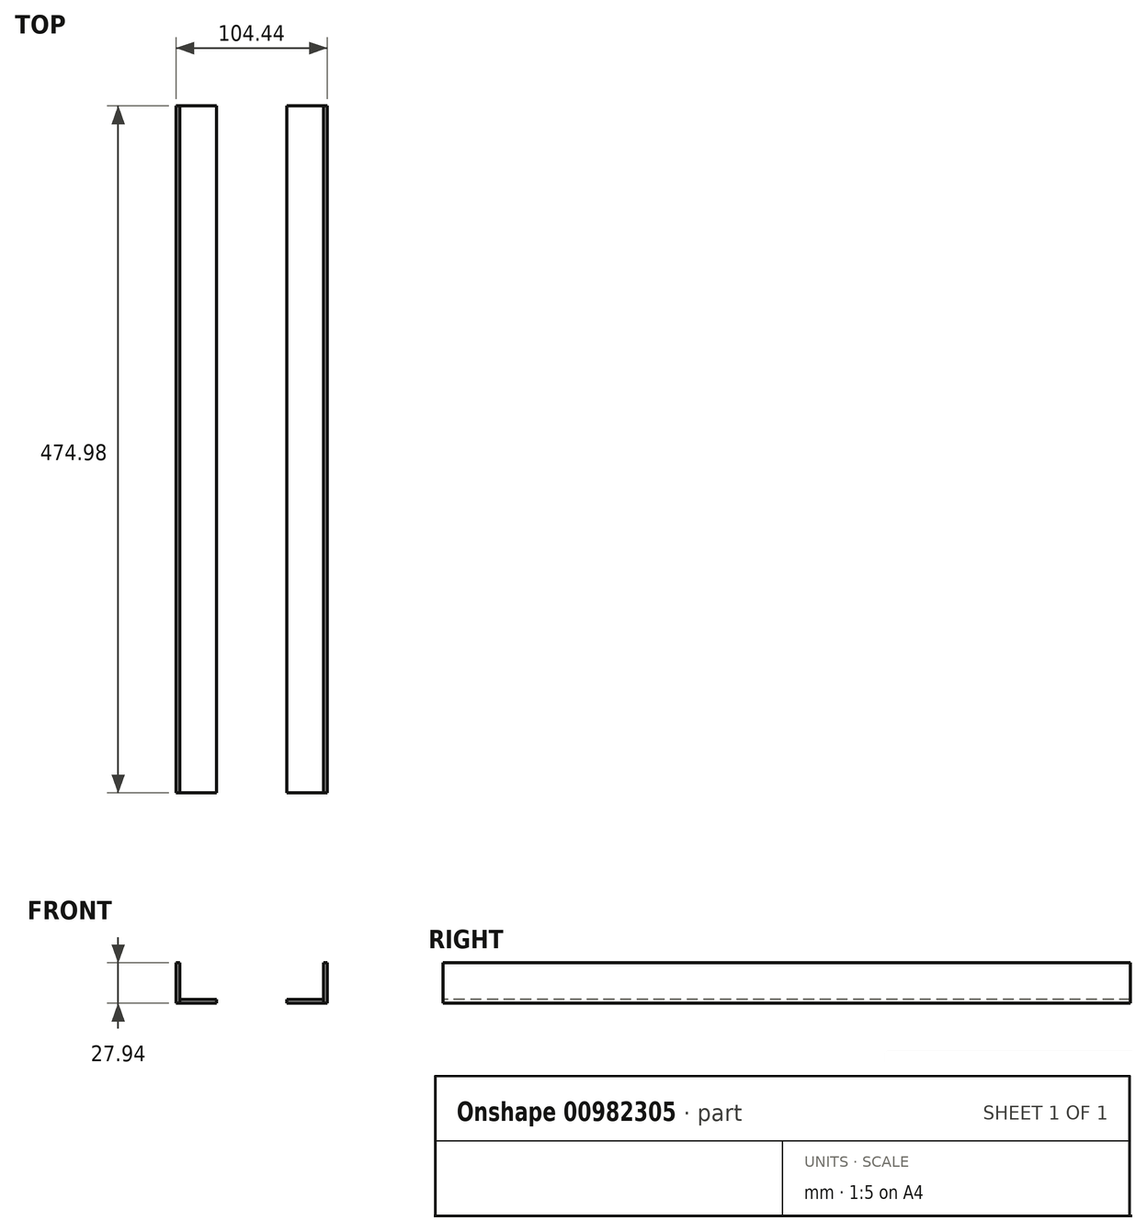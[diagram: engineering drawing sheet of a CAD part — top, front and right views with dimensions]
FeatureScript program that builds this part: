
annotation { "Feature Type Name" : "Feature", "Feature Type Description" : "" }
export const myFeature = defineFeature(function(context is Context, id is Id, definition is map)
    precondition{}
    {
        {
            var Q0;
            Q0=qCreatedBy(makeId("Top.planeOp"),FACE);
            var sketch = newSketch(context, id + "F0", { "sketchPlane" : qUnion([Q0])});
            skLineSegment(sketch, "E0.bottom", {"start": v(-84.32, 2.47) * mm, "end": v(-58.92, 2.47) * mm});
            skLineSegment(sketch, "E0.top", {"start": v(-84.32, -472.5) * mm, "end": v(-58.92, -472.5) * mm});
            skLineSegment(sketch, "E0.left", {"start": v(-84.32, 2.47) * mm, "end": v(-84.32, -472.5) * mm});
            skLineSegment(sketch, "E0.right", {"start": v(-58.92, 2.47) * mm, "end": v(-58.92, -472.5) * mm});
            skLineSegment(sketch, "E1.bottom", {"start": v(-10.36, 2.47) * mm, "end": v(15.04, 2.47) * mm});
            skLineSegment(sketch, "E1.top", {"start": v(-10.36, -472.5) * mm, "end": v(15.04, -472.5) * mm});
            skLineSegment(sketch, "E1.left", {"start": v(-10.36, 2.47) * mm, "end": v(-10.36, -472.5) * mm});
            skLineSegment(sketch, "E1.right", {"start": v(15.04, 2.47) * mm, "end": v(15.04, -472.5) * mm});
            skSolve(sketch);
        }
        {
            var Q0;
            Q0=makeQuery(id+"F0.imprint","IMPRINT",FACE,{"disambiguationData":[TD([[makeQuery(id+"F0.imprint","IMPRINT",EDGE,{"derivedFrom":sQuery(id+"F0.wireOp",EDGE,"E0.bottom")}),-1.0]])]});
            var Q1;
            Q1=makeQuery(id+"F0.imprint","IMPRINT",FACE,{"disambiguationData":[TD([[makeQuery(id+"F0.imprint","IMPRINT",EDGE,{"derivedFrom":sQuery(id+"F0.wireOp",EDGE,"E1.bottom")}),-1.0]])]});
            extrude(context, id + "F1", {"entities" : qUnion([Q0, Q1]), "depth" : 2.54 * mm, "offsetDistance" : 25.4 * mm});
        }
        {
            var Q0;
            Q0=qCreatedBy(makeId("Top.planeOp"),FACE);
            var sketch = newSketch(context, id + "F2", { "sketchPlane" : qUnion([Q0])});
            skLineSegment(sketch, "E2.0", {"start": v(-84.32, 2.47) * mm, "end": v(-84.32, -472.5) * mm});
            skLineSegment(sketch, "E3.0", {"start": v(15.04, 2.47) * mm, "end": v(15.04, -472.5) * mm});
            skLineSegment(sketch, "E4.bottom", {"start": v(-84.32, 2.47) * mm, "end": v(-86.86, 2.47) * mm});
            skLineSegment(sketch, "E4.top", {"start": v(-84.32, -472.5) * mm, "end": v(-86.86, -472.5) * mm});
            skLineSegment(sketch, "E4.right", {"start": v(-86.86, 2.47) * mm, "end": v(-86.86, -472.5) * mm});
            skLineSegment(sketch, "E5.bottom", {"start": v(15.04, 2.47) * mm, "end": v(17.58, 2.47) * mm});
            skLineSegment(sketch, "E5.top", {"start": v(15.04, -472.5) * mm, "end": v(17.58, -472.5) * mm});
            skLineSegment(sketch, "E5.right", {"start": v(17.58, 2.47) * mm, "end": v(17.58, -472.5) * mm});
            skSolve(sketch);
        }
        {
            var Q0;
            Q0=makeQuery(id+"F2.imprint","IMPRINT",FACE,{"disambiguationData":[TD([[makeQuery(id+"F2.imprint","IMPRINT",EDGE,{"derivedFrom":sQuery(id+"F2.wireOp",EDGE,"E4.bottom")}),1.0]])]});
            var Q1;
            Q1=makeQuery(id+"F2.imprint","IMPRINT",FACE,{"disambiguationData":[TD([[makeQuery(id+"F2.imprint","IMPRINT",EDGE,{"derivedFrom":sQuery(id+"F2.wireOp",EDGE,"E5.bottom")}),-1.0]])]});
            extrude(context, id + "F3", {"entities" : qUnion([Q0, Q1]), "depth" : 27.94 * mm, "offsetDistance" : 25.4 * mm});
        }
    });
